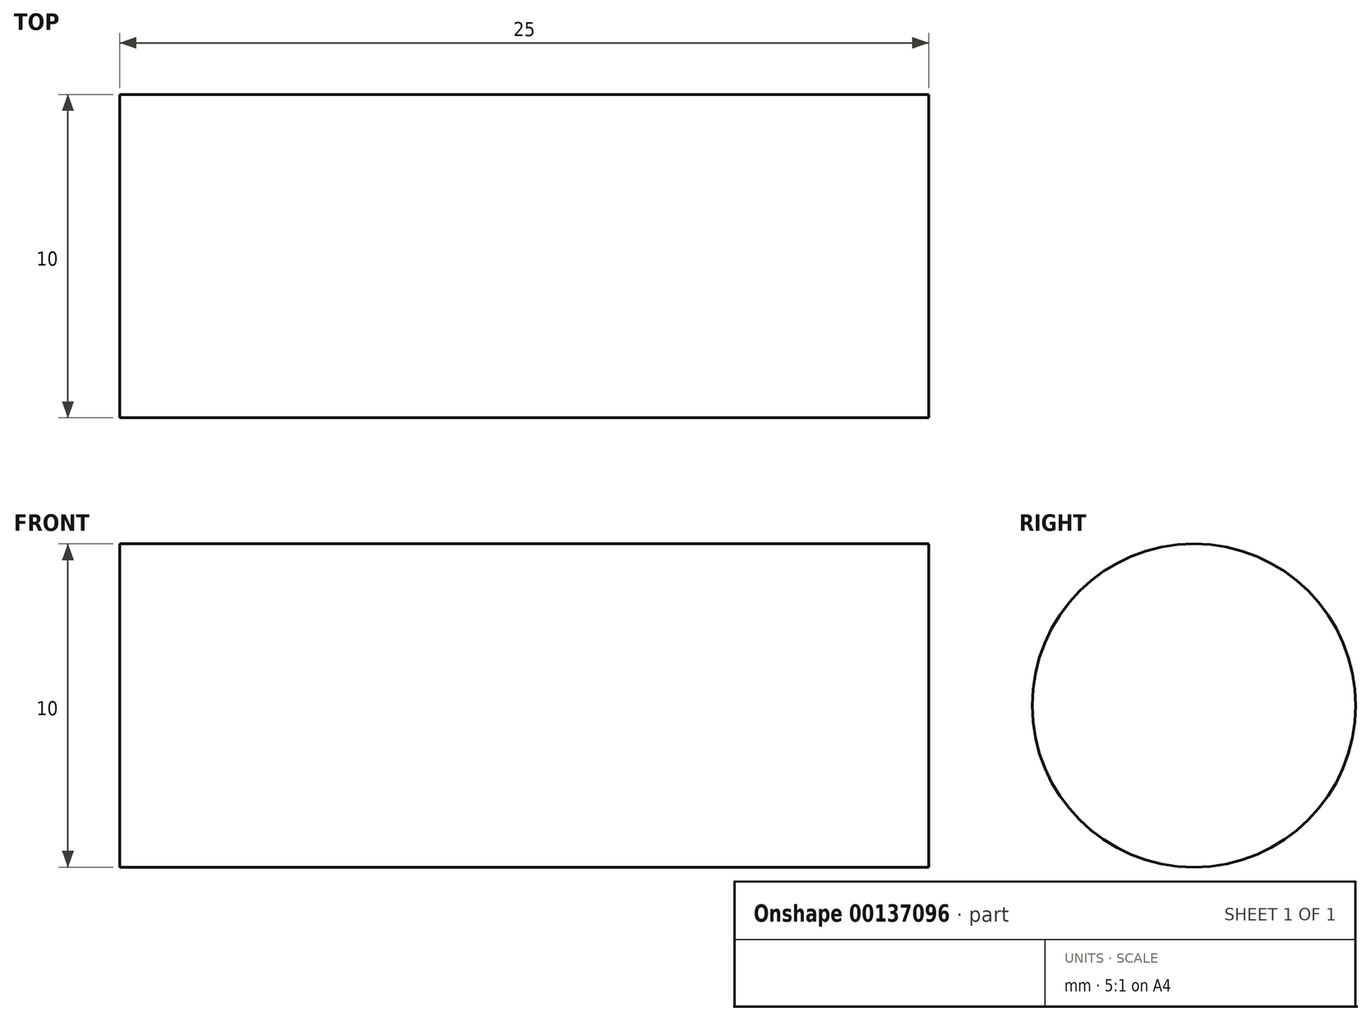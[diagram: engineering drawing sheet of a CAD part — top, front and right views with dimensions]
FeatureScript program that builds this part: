
annotation { "Feature Type Name" : "Feature", "Feature Type Description" : "" }
export const myFeature = defineFeature(function(context is Context, id is Id, definition is map)
    precondition{}
    {
        {
            var Q0;
            Q0=qCreatedBy(makeId("Right.planeOp"),FACE);
            var sketch = newSketch(context, id + "F0", { "sketchPlane" : qUnion([Q0])});
            skCircle(sketch, "E0", {"center": v(0, 0) * mm, "radius": 5 * mm});
            skSolve(sketch);
        }
        {
            var Q0;
            Q0=makeQuery(id+"F0.imprint","IMPRINT",FACE,{"disambiguationData":[TD([[makeQuery(id+"F0.imprint","IMPRINT",EDGE,{"derivedFrom":sQuery(id+"F0.wireOp",EDGE,"E0")}),1.0]])]});
            extrude(context, id + "F1", {"entities" : qUnion([Q0]), "endBound" : BoundingType.SYMMETRIC, "depth" : 25 * mm});
        }
    });
